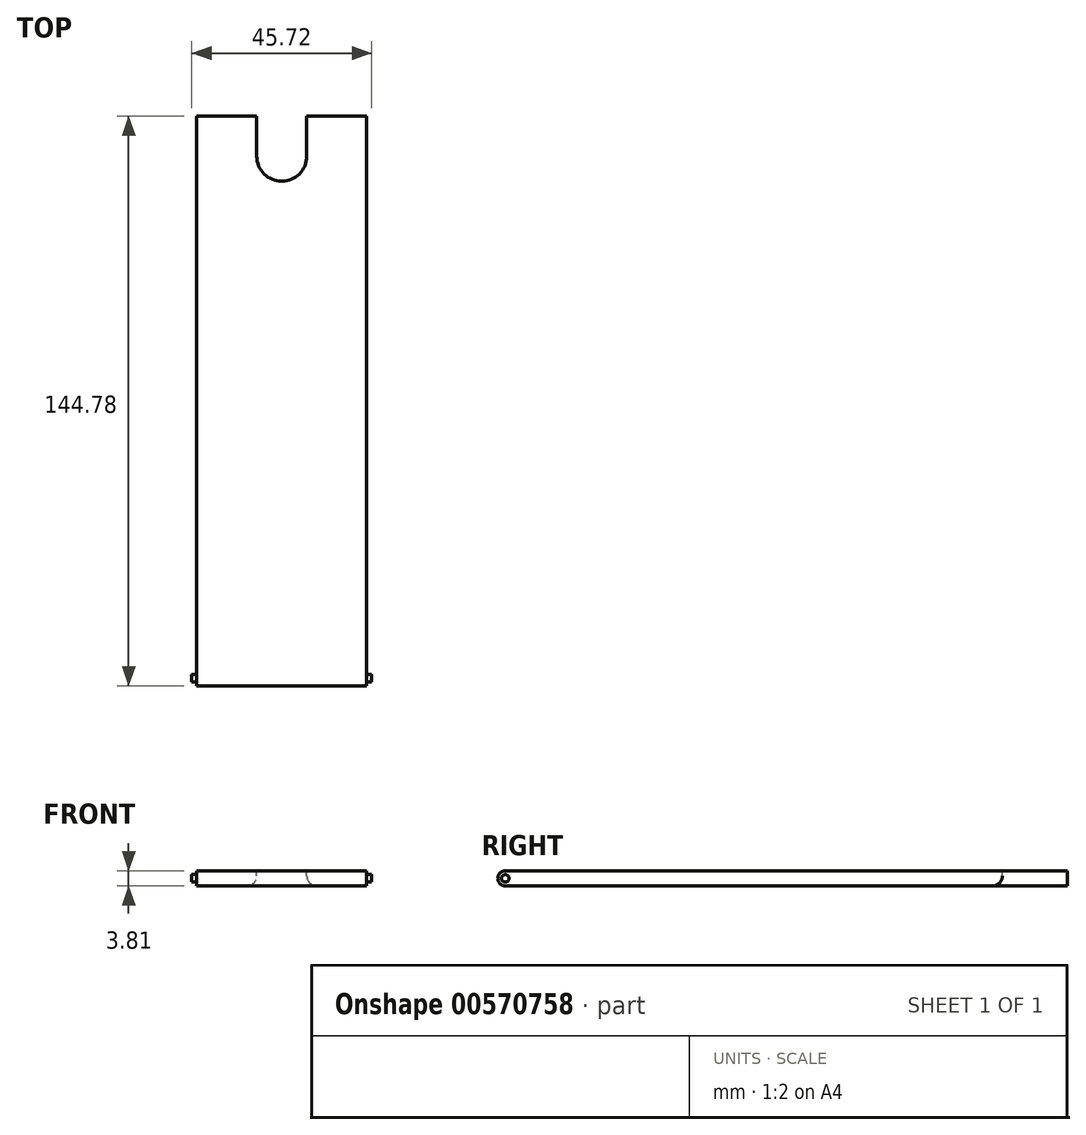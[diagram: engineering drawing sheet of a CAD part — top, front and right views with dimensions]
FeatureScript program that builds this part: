
annotation { "Feature Type Name" : "Feature", "Feature Type Description" : "" }
export const myFeature = defineFeature(function(context is Context, id is Id, definition is map)
    precondition{}
    {
        {
            var Q0;
            Q0=qCreatedBy(makeId("Top.planeOp"),FACE);
            var sketch = newSketch(context, id + "F0", { "sketchPlane" : qUnion([Q0])});
            skLineSegment(sketch, "E0.bottom", {"start": v(15.39, 68) * mm, "end": v(-27.8, 68) * mm});
            skLineSegment(sketch, "E0.top", {"start": v(15.39, -76.78) * mm, "end": v(-27.8, -76.78) * mm});
            skLineSegment(sketch, "E0.left", {"start": v(15.39, 68) * mm, "end": v(15.39, -76.78) * mm});
            skLineSegment(sketch, "E0.right", {"start": v(-27.8, 68) * mm, "end": v(-27.8, -76.78) * mm});
            skSolve(sketch);
        }
        {
            var Q0;
            Q0=makeQuery(id+"F0.imprint","IMPRINT",FACE,{"disambiguationData":[TD([[makeQuery(id+"F0.imprint","IMPRINT",EDGE,{"derivedFrom":sQuery(id+"F0.wireOp",EDGE,"E0.bottom")}),1.0]])]});
            extrude(context, id + "F1", {"entities" : qUnion([Q0]), "depth" : 3.8 * mm, "offsetDistance" : 25.4 * mm});
        }
        {
            var Q0;
            Q0=makeQuery(id+"F1.opExtrude","CAP_FACE",FACE,{"disambiguationData":[OSD([sQuery(id+"F0.wireOp",EDGE,"E0.bottom"),sQuery(id+"F0.wireOp",EDGE,"E0.top"),sQuery(id+"F0.wireOp",EDGE,"E0.left"),sQuery(id+"F0.wireOp",EDGE,"E0.right")])],"isStart":false});
            var sketch = newSketch(context, id + "F2", { "sketchPlane" : qUnion([Q0])});
            skLineSegment(sketch, "E1.bottom", {"start": v(-12.55, 68) * mm, "end": v(0.15, 68) * mm});
            skLineSegment(sketch, "E1.top", {"start": v(-12.55, 57.8) * mm, "end": v(0.15, 57.8) * mm});
            skLineSegment(sketch, "E1.left", {"start": v(-12.55, 68) * mm, "end": v(-12.55, 57.8) * mm});
            skLineSegment(sketch, "E1.right", {"start": v(0.15, 68) * mm, "end": v(0.15, 57.8) * mm});
            skCircle(sketch, "E2", {"center": v(-6.2, 57.8) * mm, "radius": 6.35 * mm});
            skSolve(sketch);
        }
        {
            var Q0;
            {var subQ0=sQuery(id+"F2.wireOp",EDGE,"E1.top");Q0=makeQuery(id+"F2.imprint","IMPRINT",FACE,{"disambiguationData":[TD([[makeQuery(id+"F2.imprint","IMPRINT",EDGE,{"derivedFrom":subQ0}),1.0]])]});}
            var Q1;
            Q1=makeQuery(id+"F2.imprint","IMPRINT",FACE,{"disambiguationData":[TD([[makeQuery(id+"F2.imprint","IMPRINT",EDGE,{"derivedFrom":sQuery(id+"F2.wireOp",EDGE,"E1.bottom")}),1.0]])]});
            var Q2;
            {var subQ0=sQuery(id+"F2.wireOp",EDGE,"E1.top");Q2=makeQuery(id+"F2.imprint","IMPRINT",FACE,{"disambiguationData":[TD([[makeQuery(id+"F2.imprint","IMPRINT",EDGE,{"derivedFrom":subQ0}),-1.0]])]});}
            extrude(context, id + "F3", {"entities" : qUnion([Q0, Q1, Q2]), "operationType" : NewBodyOperationType.REMOVE, "oppositeDirection" : true, "depth" : 25.4 * mm, "offsetDistance" : 25.4 * mm});
        }
        {
            var Q0;
            Q0=makeQuery(id+"F3.boolean.opBoolean","COPY",EDGE,{"derivedFrom":makeQuery(id+"F3.opExtrude","CAP_EDGE",EDGE,{"disambiguationData":[OSD([sQuery(id+"F2.wireOp",EDGE,"E1.left")])],"isStart":true})});
            var Q1;
            Q1=makeQuery(id+"F3.boolean.opBoolean","INTERSECT",EDGE,{"derivedFrom":[makeQuery(id+"F1.opExtrude","CAP_FACE",FACE,{"disambiguationData":[OSD([sQuery(id+"F0.wireOp",EDGE,"E0.bottom"),sQuery(id+"F0.wireOp",EDGE,"E0.top"),sQuery(id+"F0.wireOp",EDGE,"E0.left"),sQuery(id+"F0.wireOp",EDGE,"E0.right")])],"isStart":true}),makeQuery(id+"F3.opExtrude","SWEPT_FACE",FACE,{"disambiguationData":[OSD([sQuery(id+"F2.wireOp",EDGE,"E1.left")])]})]});
            fillet(context, id + "F4", {"entities" : qUnion([Q0, Q1]), "radius" : 2.54 * mm, "tangentPropagation" : true, "allowEdgeOverflow" : false});
        }
        {
            var Q0;
            Q0=makeQuery(id+"F1.opExtrude","CAP_EDGE",EDGE,{"disambiguationData":[OSD([sQuery(id+"F0.wireOp",EDGE,"E0.top")])],"isStart":false});
            var Q1;
            Q1=makeQuery(id+"F1.opExtrude","CAP_EDGE",EDGE,{"disambiguationData":[OSD([sQuery(id+"F0.wireOp",EDGE,"E0.top")])],"isStart":true});
            fillet(context, id + "F5", {"entities" : qUnion([Q0, Q1]), "radius" : 1.9 * mm, "tangentPropagation" : true, "allowEdgeOverflow" : false});
        }
        {
            var Q0;
            Q0=makeQuery(id+"F1.opExtrude","SWEPT_FACE",FACE,{"disambiguationData":[OSD([sQuery(id+"F0.wireOp",EDGE,"E0.right")])]});
            var sketch = newSketch(context, id + "F6", { "sketchPlane" : qUnion([Q0])});
            skPoint(sketch, "E3", {"position": v(74.87, 1.9) * mm});
            skCircle(sketch, "E4", {"center": v(74.87, 1.9) * mm, "radius": 0.95 * mm});
            skSolve(sketch);
        }
        {
            var Q0;
            Q0=makeQuery(id+"F6.imprint","IMPRINT",FACE,{"disambiguationData":[TD([[makeQuery(id+"F6.imprint","IMPRINT",EDGE,{"derivedFrom":sQuery(id+"F6.wireOp",EDGE,"E4")}),1.0]])]});
            extrude(context, id + "F7", {"entities" : qUnion([Q0]), "operationType" : NewBodyOperationType.ADD, "depth" : 1.27 * mm, "offsetDistance" : 25.4 * mm, "hasSecondDirection" : true, "secondDirectionOppositeDirection" : true, "secondDirectionDepth" : 44.45 * mm});
        }
    });
